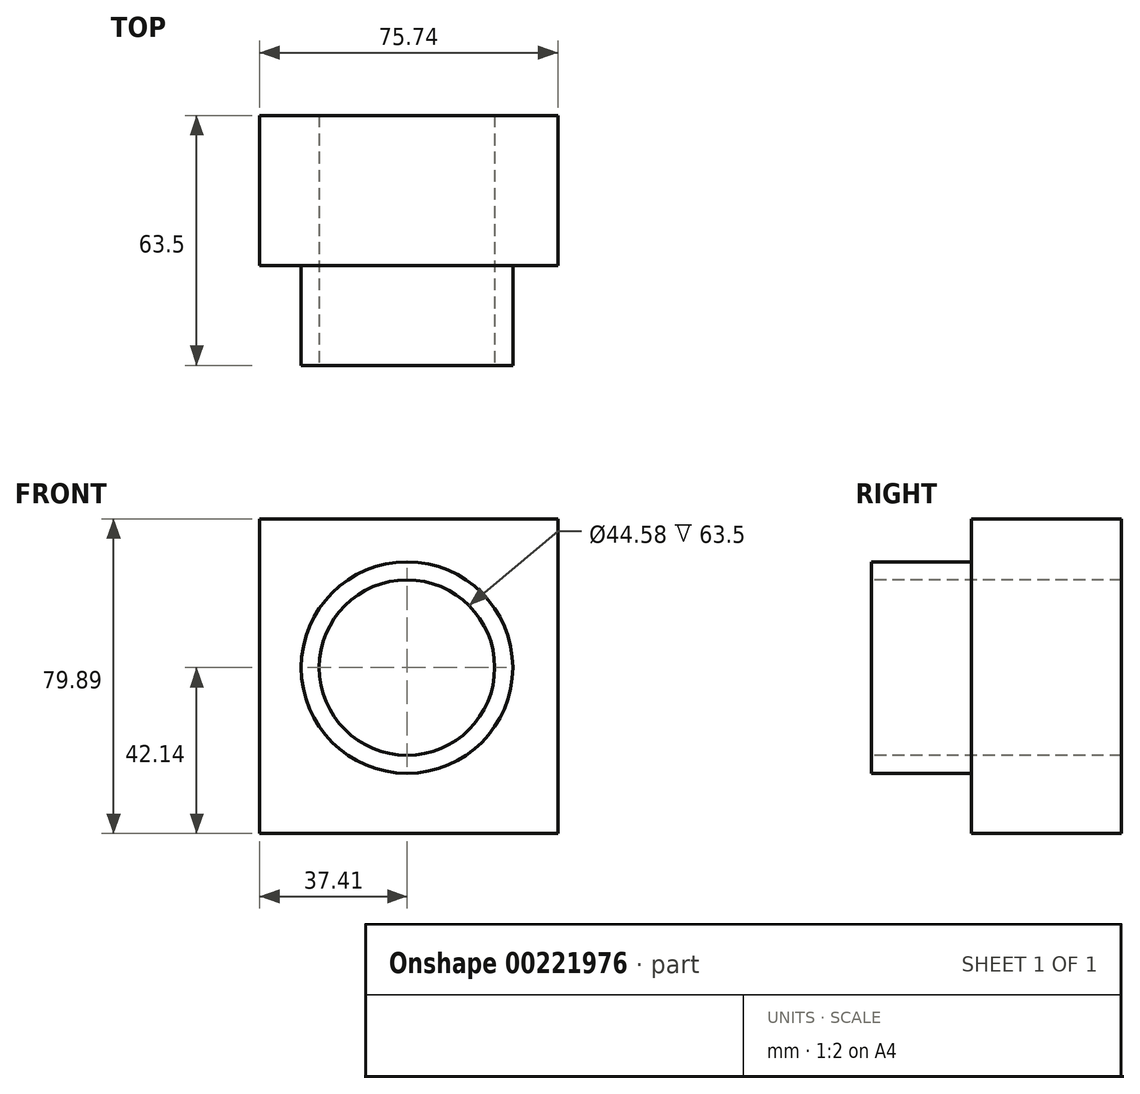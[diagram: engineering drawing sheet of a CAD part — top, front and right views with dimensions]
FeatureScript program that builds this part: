
annotation { "Feature Type Name" : "Feature", "Feature Type Description" : "" }
export const myFeature = defineFeature(function(context is Context, id is Id, definition is map)
    precondition{}
    {
        {
            var Q0;
            Q0=qCreatedBy(makeId("Front.planeOp"),FACE);
            var sketch = newSketch(context, id + "F0", { "sketchPlane" : qUnion([Q0])});
            skLineSegment(sketch, "E0.bottom", {"start": v(-37.4, 37.75) * mm, "end": v(38.33, 37.75) * mm});
            skLineSegment(sketch, "E0.top", {"start": v(-37.4, -42.14) * mm, "end": v(38.33, -42.14) * mm});
            skLineSegment(sketch, "E0.left", {"start": v(-37.4, 37.75) * mm, "end": v(-37.4, -42.14) * mm});
            skLineSegment(sketch, "E0.right", {"start": v(38.33, 37.75) * mm, "end": v(38.33, -42.14) * mm});
            skSolve(sketch);
        }
        {
            var Q0;
            Q0 = qSketchRegion(id + "F0", true);
            extrude(context, id + "F1", {"entities" : qUnion([Q0]), "depth" : 38.1 * mm});
        }
        {
            var Q0;
            Q0=makeQuery(id+"F1.opExtrude","CAP_FACE",FACE,{"disambiguationData":[OSD([sQuery(id+"F0.wireOp",EDGE,"E0.bottom"),sQuery(id+"F0.wireOp",EDGE,"E0.top"),sQuery(id+"F0.wireOp",EDGE,"E0.left"),sQuery(id+"F0.wireOp",EDGE,"E0.right")])],"isStart":false});
            var sketch = newSketch(context, id + "F2", { "sketchPlane" : qUnion([Q0])});
            skCircle(sketch, "E1", {"center": v(0, 0) * mm, "radius": 26.88 * mm});
            skSolve(sketch);
        }
        {
            var Q0;
            Q0 = qSketchRegion(id + "F2", true);
            extrude(context, id + "F3", {"entities" : qUnion([Q0]), "operationType" : NewBodyOperationType.ADD, "depth" : 25.4 * mm});
        }
        {
            var Q0;
            Q0=makeQuery(id+"F3.opExtrude","CAP_FACE",FACE,{"disambiguationData":[OSD([sQuery(id+"F2.wireOp",EDGE,"E1")])],"isStart":false});
            var sketch = newSketch(context, id + "F4", { "sketchPlane" : qUnion([Q0])});
            skCircle(sketch, "E2", {"center": v(0, 0) * mm, "radius": 22.29 * mm});
            skSolve(sketch);
        }
        {
            var Q0;
            Q0 = qSketchRegion(id + "F4", true);
            extrude(context, id + "F5", {"entities" : qUnion([Q0]), "operationType" : NewBodyOperationType.REMOVE, "endBound" : BoundingType.THROUGH_ALL, "oppositeDirection" : true, "depth" : 76.2 * mm});
        }
    });
